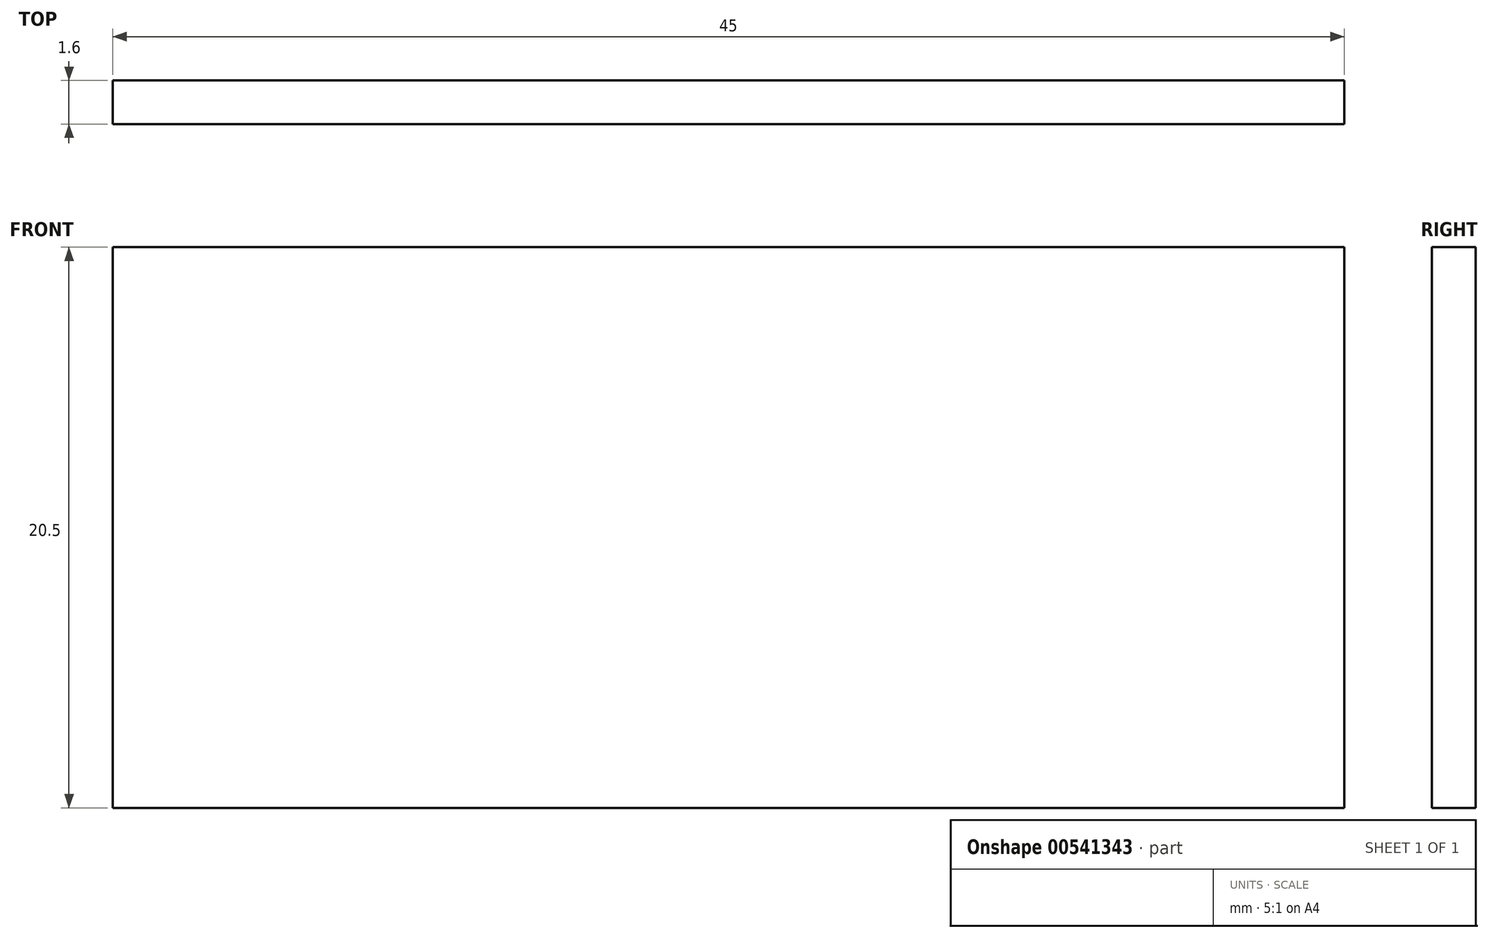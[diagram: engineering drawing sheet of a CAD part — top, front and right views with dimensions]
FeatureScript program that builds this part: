
annotation { "Feature Type Name" : "Feature", "Feature Type Description" : "" }
export const myFeature = defineFeature(function(context is Context, id is Id, definition is map)
    precondition{}
    {
        {
            var Q0;
            Q0=qCreatedBy(makeId("Front.planeOp"),FACE);
            var sketch = newSketch(context, id + "F0", { "sketchPlane" : qUnion([Q0])});
            skLineSegment(sketch, "E0.bottom", {"start": v(22.5, -10.25) * mm, "end": v(-22.5, -10.25) * mm});
            skLineSegment(sketch, "E0.top", {"start": v(22.5, 10.25) * mm, "end": v(-22.5, 10.25) * mm});
            skLineSegment(sketch, "E0.left", {"start": v(22.5, -10.25) * mm, "end": v(22.5, 10.25) * mm});
            skLineSegment(sketch, "E0.right", {"start": v(-22.5, -10.25) * mm, "end": v(-22.5, 10.25) * mm});
            skPoint(sketch, "E0.middle", {"position": v(0, 0) * mm});
            skLineSegment(sketch, "E1.left", {"start": v(-6.47, -27.28) * mm, "end": v(-6.47, -27.84) * mm});
            skLineSegment(sketch, "E1.right", {"start": v(6.47, -27.28) * mm, "end": v(6.47, -27.84) * mm});
            skPoint(sketch, "E1.middle", {"position": v(0, -27.56) * mm});
            skSolve(sketch);
        }
        {
            var Q0;
            Q0=makeQuery(id+"F0.imprint","IMPRINT",FACE,{"disambiguationData":[TD([[makeQuery(id+"F0.imprint","IMPRINT",EDGE,{"derivedFrom":sQuery(id+"F0.wireOp",EDGE,"E0.bottom")}),-1.0]])]});
            extrude(context, id + "F1", {"entities" : qUnion([Q0]), "depth" : 1.6 * mm, "offsetDistance" : 25.4 * mm});
        }
    });
